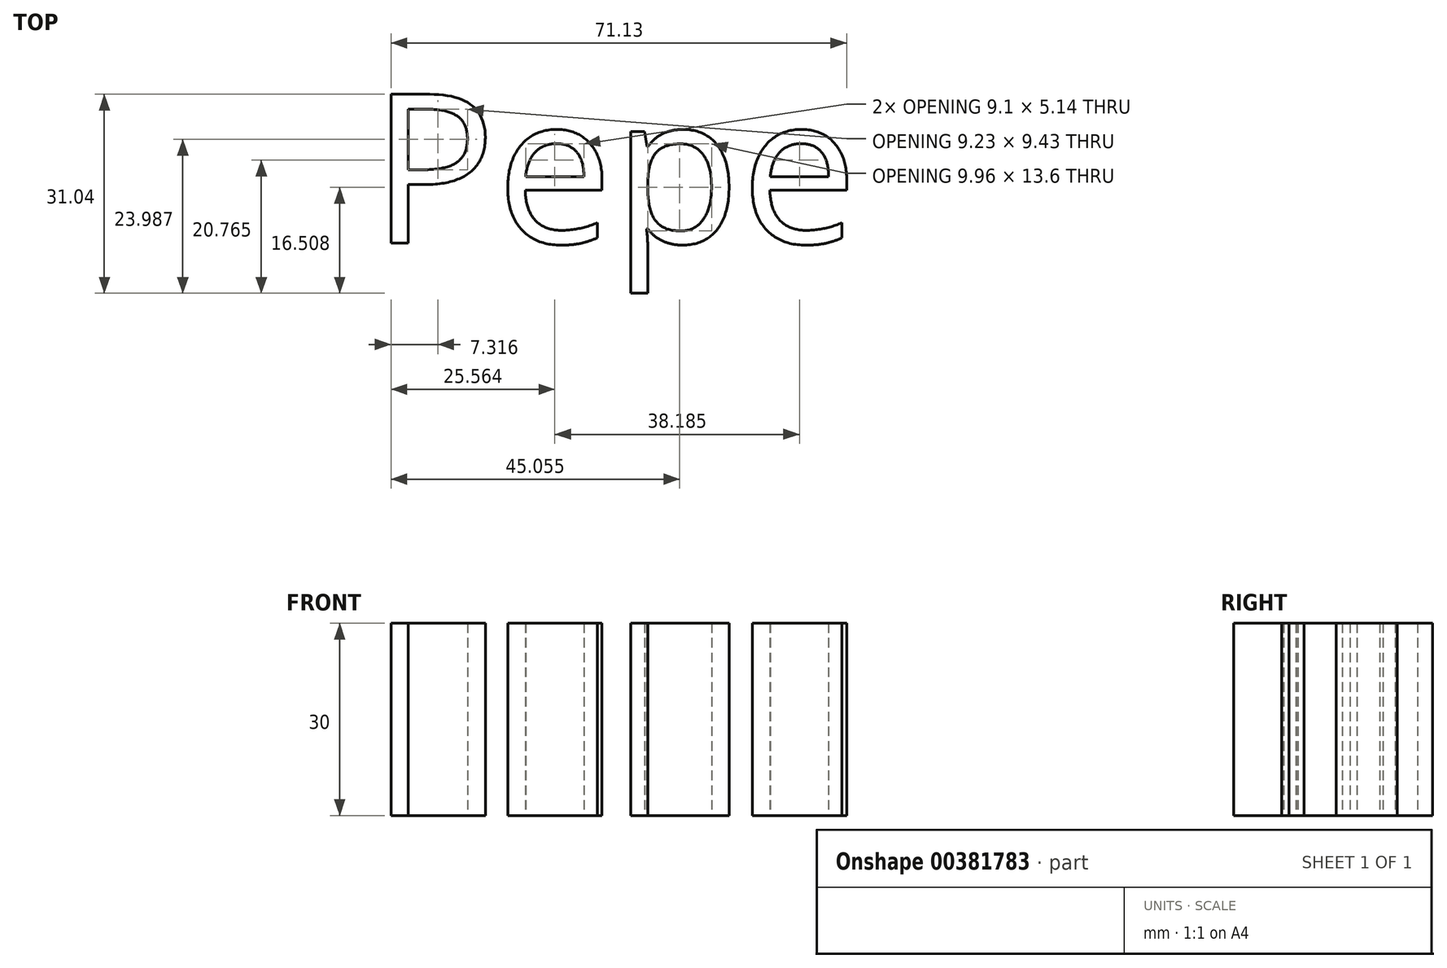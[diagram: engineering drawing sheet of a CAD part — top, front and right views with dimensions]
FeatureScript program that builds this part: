
annotation { "Feature Type Name" : "Feature", "Feature Type Description" : "" }
export const myFeature = defineFeature(function(context is Context, id is Id, definition is map)
    precondition{}
    {
        {
            var Q0;
            Q0=qCreatedBy(makeId("Top.planeOp"),FACE);
            var sketch = newSketch(context, id + "F0", { "sketchPlane" : qUnion([Q0])});
            skText(sketch, "E0", { "text": "Pepe", "fontName": "OpenSans-Regular.ttf"});
            const initialGuessF0  = {"E0": [-0.03103, 0.00548, 1, 0, 0.02342]};
            skSetInitialGuess(sketch, initialGuessF0);
            skSolve(sketch);
        }
        {
            var Q0;
            Q0 = qSketchRegion(id + "F0", true);
            extrude(context, id + "F1", {"entities" : qUnion([Q0]), "depth" : 30 * mm});
        }
    });
